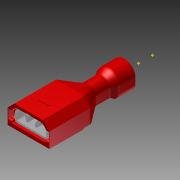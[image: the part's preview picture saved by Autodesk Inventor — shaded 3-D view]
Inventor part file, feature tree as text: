
AUTODESK INVENTOR PART (.ipt)
format: ipt  version: 2011 (Build 150239000, 239)  size: 563,712 bytes
history: native  units: in
note: dims shown in document units (in); Inventor stores cm internally (conversion verified against a paired STEP export)
features: other x4, plane x2, imported_body x1, sketch x1
ambient origin geometry x8: Origin, YZ Plane, XZ Plane, XY Plane, X Axis, Y Axis, Z Axis, Center Point
bodies: Solid1 (feature_tree)
feature tree (8):
  imported_body  "Base1"
  sketch  "Sketch1"  dims[d0=0.125in d1=0.25in]
  other  "Work Point2"
  other  "Work Point3"
  plane  "Work Plane1"
  other  "Work Axis1"
  plane  "Work Plane2"
  other  "Work Axis2"
